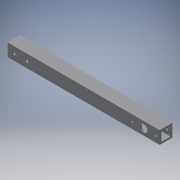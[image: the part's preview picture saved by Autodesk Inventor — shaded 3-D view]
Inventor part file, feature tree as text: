
AUTODESK INVENTOR PART (.ipt)
format: ipt  version: 2016 (Build 200138000, 138)  size: 126,976 bytes
history: native  units: in
note: dims shown in document units (in); Inventor stores cm internally (conversion verified against a paired STEP export)
features: extrude x2, sketch x2
ambient origin geometry x8: Origin, YZ Plane, XZ Plane, XY Plane, X Axis, Y Axis, Z Axis, Center Point
bodies: Solid1 (feature_tree)
feature tree (4):
  extrude  "Extrusion1"  Depth=1.0in
  extrude  "Extrusion2"  Depth=12.0in TaperAngle=0.0deg
  sketch  "Sketch1"  dims[d0=1.0in d1=1.0in]
  sketch  "Sketch2"  dims[d2=0.125in d3=12.0in d4=0.0in d5=1.875in d6=0.5in d7=1.25in d8=0.2in d9=0.2in d10=0.5in d11=1.0in d12=0.0in d13=0.25in d14=0.25in d15=0.5in d16=1.0in]
